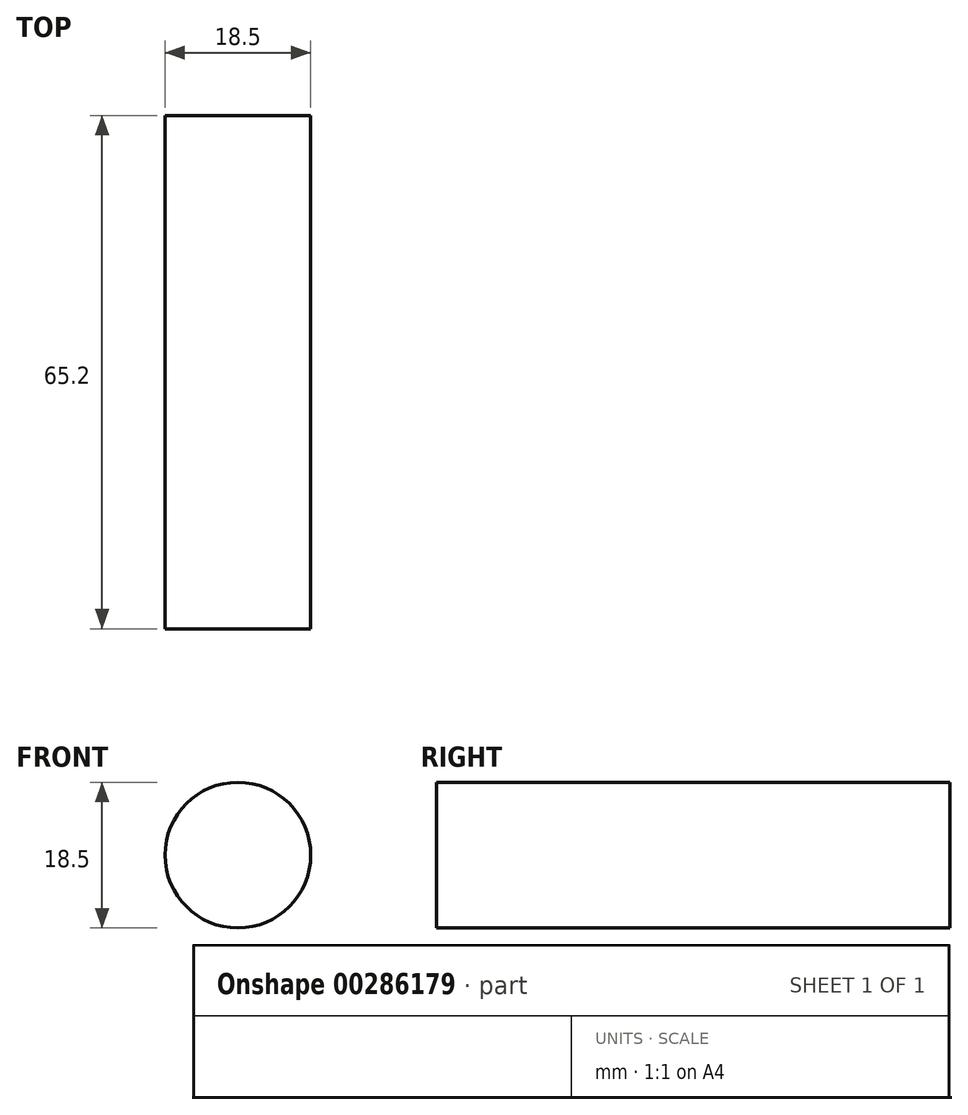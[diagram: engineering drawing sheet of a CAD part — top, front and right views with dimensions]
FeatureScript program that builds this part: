
annotation { "Feature Type Name" : "Feature", "Feature Type Description" : "" }
export const myFeature = defineFeature(function(context is Context, id is Id, definition is map)
    precondition{}
    {
        {
            var Q0;
            Q0=qCreatedBy(makeId("Front.planeOp"),FACE);
            var sketch = newSketch(context, id + "F0", { "sketchPlane" : qUnion([Q0])});
            skCircle(sketch, "E0", {"center": v(0, 0) * mm, "radius": 9.25 * mm});
            skSolve(sketch);
        }
        {
            var Q0;
            Q0=makeQuery(id+"F0.imprint","IMPRINT",FACE,{"disambiguationData":[TD([[makeQuery(id+"F0.imprint","IMPRINT",EDGE,{"derivedFrom":sQuery(id+"F0.wireOp",EDGE,"E0")}),1.0]])]});
            extrude(context, id + "F1", {"entities" : qUnion([Q0]), "depth" : 65.2 * mm});
        }
    });
